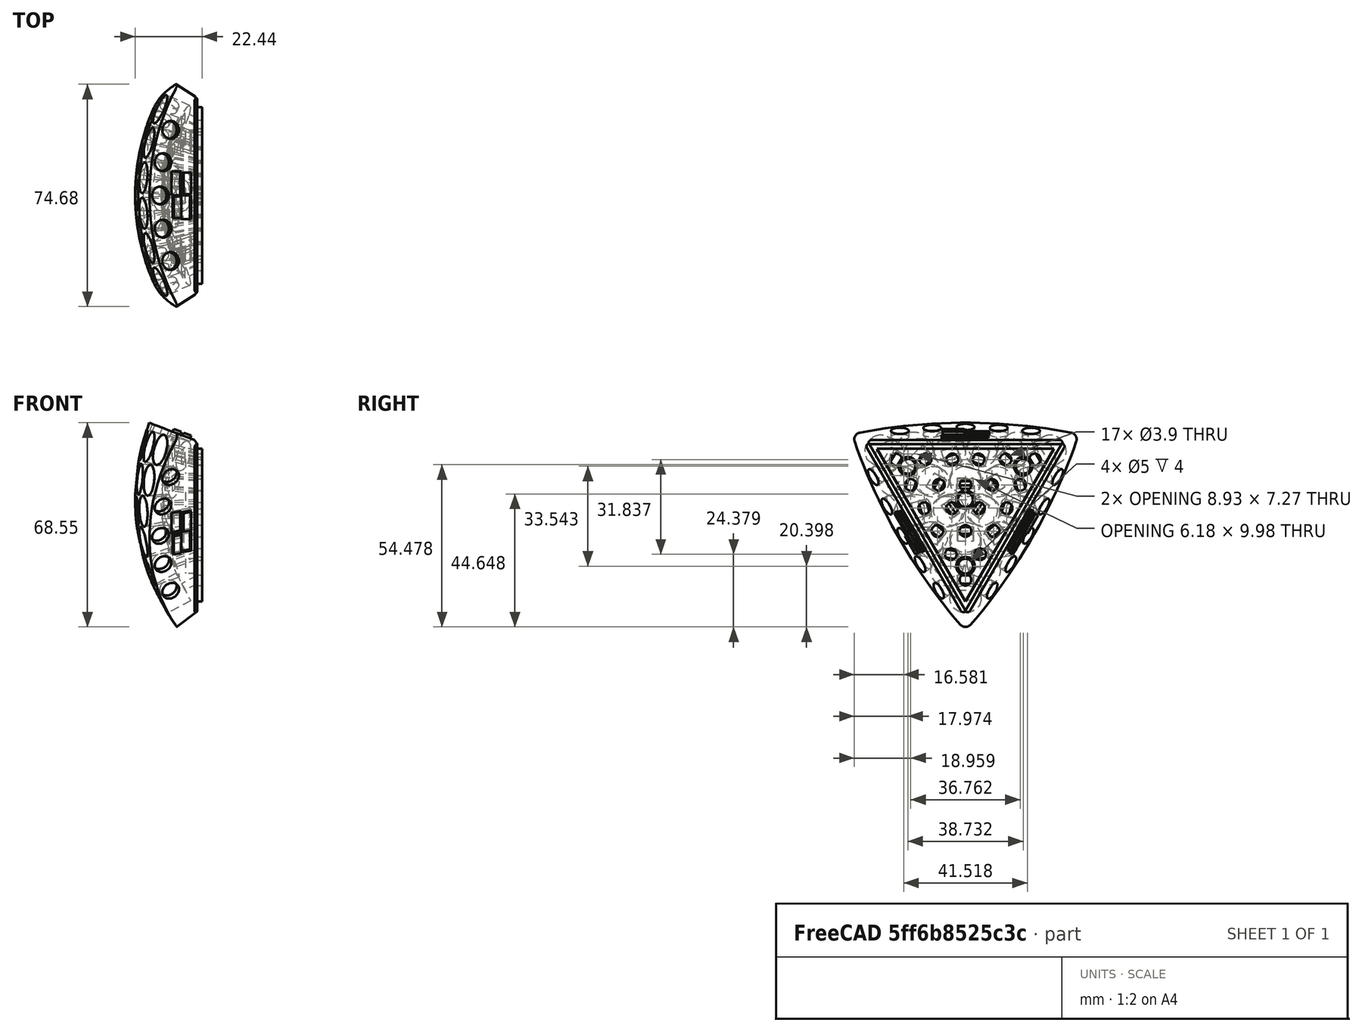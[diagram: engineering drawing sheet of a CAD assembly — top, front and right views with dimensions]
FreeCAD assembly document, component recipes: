
FREECAD ASSEMBLY — COMPONENT RECIPES ("Shell_and_PCB_complete")

This assembly document has 15 components, labeled P0..P14 below (a component is one placed body or linked part). 15 of them carry a construction recipe — the FreeCAD feature program that regenerates the part from scratch, quoted from this document or its linked companion documents; the rest are supplied as boundary geometry only. No exploded tour is included for this assembly.
COMPONENT P0 — recipe-attached ("shell001", modeled in this document).
Construction recipe (the document's own serialized feature program — sketch geometry with constraints, then the solid features built on it; lengths are millimeters unless a unit is written):

FEATURE [PartDesign::FeatureBase] BaseFeature
  BaseFeature = -> Fillet
FEATURE [PartDesign::CoordinateSystem] Local_CS
  AttacherType = Attacher::AttachEngine3D
  MapMode = 11
  Placement = pos=(-63.7856,-7e-15,24.3639) rot=(0.701166,0.701166,-0.129353;3.39887rad)
  Support = -> [BaseFeature]
FEATURE [PartDesign::CoordinateSystem] Local_CS001
  AttacherType = Attacher::AttachEngine3D
  MapMode = 11
  Placement = pos=(-63.7856,-21.0998,-12.182) rot=(-0.317298,-0.615291,-0.721622;1.68298rad)
  Support = -> [BaseFeature]
FEATURE [PartDesign::CoordinateSystem] Local_CS002
  AttacherType = Attacher::AttachEngine3D
  MapMode = 11
  Placement = pos=(-63.7856,21.0998,-12.182) rot=(0.544291,0.280684,-0.790546;2.00531rad)
  Support = -> [BaseFeature]
FEATURE [PartDesign::CoordinateSystem] Local_CS003
  AttacherType = Attacher::AttachEngine3D
  MapMode = 11
  Placement = pos=(-60.3757,8.95889,-30.6057) rot=(0.544291,0.280684,-0.790546;2.00531rad)
  Support = -> [BaseFeature]
FEATURE [PartDesign::CoordinateSystem] Local_CS004
  AttacherType = Attacher::AttachEngine3D
  MapMode = 11
  Placement = pos=(-60.3757,30.9848,7.54423) rot=(0.544291,0.280684,-0.790546;2.00531rad)
  Support = -> [BaseFeature]
FEATURE [PartDesign::CoordinateSystem] Local_CS005
  AttacherType = Attacher::AttachEngine3D
  MapMode = 11
  Placement = pos=(-60.3757,-8.95889,-30.6057) rot=(-0.317298,-0.615291,-0.721622;1.68298rad)
  Support = -> [BaseFeature]
FEATURE [PartDesign::CoordinateSystem] Local_CS006
  AttacherType = Attacher::AttachEngine3D
  MapMode = 11
  Placement = pos=(-60.3757,-30.9848,7.54423) rot=(-0.317298,-0.615291,-0.721622;1.68298rad)
  Support = -> [BaseFeature]
FEATURE [PartDesign::CoordinateSystem] Local_CS007
  AttacherType = Attacher::AttachEngine3D
  MapMode = 11
  Placement = pos=(-60.3757,-22.0259,23.0615) rot=(0.701166,0.701166,-0.129353;3.39887rad)
  Support = -> [BaseFeature]
FEATURE [PartDesign::CoordinateSystem] Local_CS008
  AttacherType = Attacher::AttachEngine3D
  MapMode = 11
  Placement = pos=(-60.3757,22.0259,23.0615) rot=(0.701166,0.701166,-0.129353;3.39887rad)
  Support = -> [BaseFeature]
FEATURE [PartDesign::CoordinateSystem] Local_CS009
  AttacherType = Attacher::AttachEngine3D
  MapMode = 11
  Placement = pos=(-51.4379,-19.3661,11.181) rot=(0.57735,0.57735,-0.57735;4.18879rad)
  Support = -> [BaseFeature]
FEATURE [PartDesign::CoordinateSystem] Local_CS010
  AttacherType = Attacher::AttachEngine3D
  MapMode = 11
  Placement = pos=(-51.4379,19.3661,11.181) rot=(0.57735,0.57735,-0.57735;4.18879rad)
  Support = -> [BaseFeature]
FEATURE [PartDesign::CoordinateSystem] Local_CS011
  AttacherType = Attacher::AttachEngine3D
  MapMode = 11
  Placement = pos=(-51.4379,0,-22.362) rot=(0.57735,0.57735,-0.57735;4.18879rad)
  Support = -> [BaseFeature]
FEATURE [PartDesign::CoordinateSystem] Local_CS012
  AttacherType = Attacher::AttachEngine3D
  MapMode = 11
  Placement = pos=(-51.4379,2e-15,1.69e-14) rot=(0.57735,0.57735,-0.57735;4.18879rad)
  Support = -> [BaseFeature]
FEATURE [PartDesign::Body] Body  label="shell"
  BaseFeature = -> Fillet
  Group = -> [BaseFeature,Local_CS,Local_CS001,Local_CS002,Local_CS003,Local_CS004,Local_CS005,Local_CS006,Local_CS007,Local_CS008,Local_CS009,Local_CS010,Local_CS011,Local_CS012]
  Origin = -> Origin
  Tip = -> BaseFeature
COMPONENT P1 — same part as P0; its construction recipe is shown at P0.
COMPONENT P2 — same part as P0; its construction recipe is shown at P0.
COMPONENT P3 — same part as P0; its construction recipe is shown at P0.
COMPONENT P4 — same part as P0; its construction recipe is shown at P0.
COMPONENT P5 — same part as P0; its construction recipe is shown at P0.
COMPONENT P6 — same part as P0; its construction recipe is shown at P0.
COMPONENT P7 — same part as P0; its construction recipe is shown at P0.
COMPONENT P8 — same part as P0; its construction recipe is shown at P0.
COMPONENT P9 — same part as P0; its construction recipe is shown at P0.
COMPONENT P10 — same part as P0; its construction recipe is shown at P0.
COMPONENT P11 — same part as P0; its construction recipe is shown at P0.
COMPONENT P12 — same part as P0; its construction recipe is shown at P0.
COMPONENT P13 — same part as P0; its construction recipe is shown at P0.
COMPONENT P14 — same part as P0; its construction recipe is shown at P0.
PROVENANCE & LICENSES
A FreeCAD (.FCStd) document from a public repository crawl; recipes are the document's own serialized feature recipes (and, for linked parts, companion documents' recipes).
License: as declared in the source repository (recorded in the dataset sidecar).
